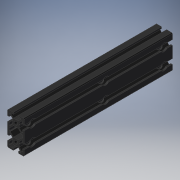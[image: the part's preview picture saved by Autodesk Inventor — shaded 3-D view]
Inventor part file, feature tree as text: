
AUTODESK INVENTOR PART (.ipt)
format: ipt  version: 2019 (Build 230136000, 136)  size: 398,848 bytes
history: native  units: mm
features: other x10, revolve x6, sketch x5, extrude x1, hole x1, pattern_linear x1
ambient origin geometry x8: Origin, YZ Plane, XZ Plane, XY Plane, X Axis, Y Axis, Z Axis, Center Point
bodies: Solid1 (feature_tree)
feature tree (24):
  extrude  "Extrusion1"  Depth=10.0mm TaperAngle=0.0deg
  hole  "Hole1"  [1 undecoded]
  pattern_linear  "Rectangular Pattern1"  Spacing1=360.0deg  [1 undecoded]
  revolve  "Revolution1"  Angle=360.0deg
  revolve  "Revolution2"  [1 undecoded]
  revolve  "Revolution3"  [1 undecoded]
  revolve  "Revolution4"  [1 undecoded]
  revolve  "Revolution5"  [1 undecoded]
  revolve  "Revolution6"  [1 undecoded]
  other  "C1_XY"
  other  "C1_YZ"
  other  "C1_ZX"
  other  "C1_X"
  other  "C1_Y"
  other  "C1_Z"
  other  "C1_Center"
  sketch  "Sketch_1"  dims[d0=180.0mm d1=0.0mm]
  sketch  "Sketch2"  dims[d2=4.2mm d3=6.0mm d4=4.0mm d5=2.0mm d6=90.0deg d7=180.0mm d8=0.0mm d9=20.0mm d11=20.0mm d12=10.0mm d14=0.0mm]
  sketch  "Sketch_50"  dims[d15=360.0deg d16=360.0deg]
  other  "_p_______27_Sketch_50_0"
  sketch  "Sketch_51"  dims[d17=360.0deg]
  other  "_p_______28_Sketch_51_0"
  sketch  "Sketch_52"  dims[d18=360.0deg d19=360.0deg d20=360.0deg d21=0.0mm]
  other  "_p_______29_Sketch_52_0"
note: 7 required parameter values undecoded (feature->parameter linkage not recoverable at this tier; creation-order binding heuristic only, values carry confidence <= 0.55)